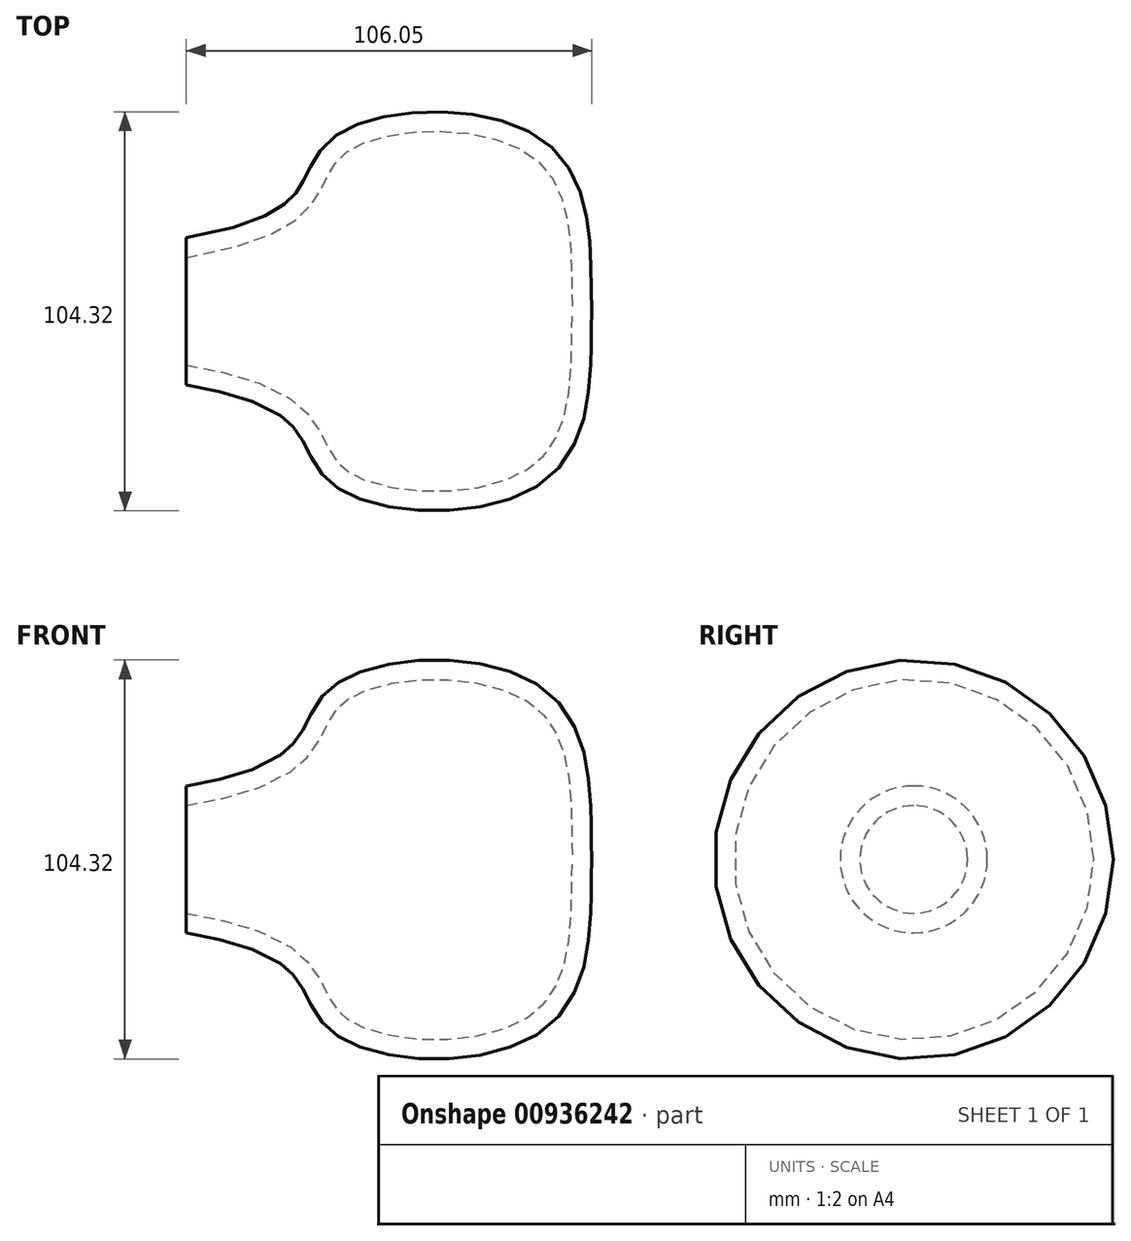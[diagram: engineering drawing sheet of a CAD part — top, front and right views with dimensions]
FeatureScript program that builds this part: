
annotation { "Feature Type Name" : "Feature", "Feature Type Description" : "" }
export const myFeature = defineFeature(function(context is Context, id is Id, definition is map)
    precondition{}
    {
        {
            var Q0;
            Q0=qCreatedBy(makeId("Top.planeOp"),FACE);
            var sketch = newSketch(context, id + "F0", { "sketchPlane" : qUnion([Q0])});
            skPoint(sketch, "E0", {"position": v(-54.13, 14.08) * mm});
            skPoint(sketch, "E1", {"position": v(-12.42, 41.47) * mm});
            skPoint(sketch, "E2", {"position": v(37.07, 39.92) * mm});
            skPoint(sketch, "E3", {"position": v(46.84, 0) * mm});
            skFitSpline(sketch, "E4", {"points": [v(-54.13, 14.08) * mm, v(-12.42, 41.47) * mm, v(37.07, 39.92) * mm, v(46.84, 0) * mm], "startDerivative": vector(352.1, 57.3) * mm, "endDerivative": vector(5.97, -126.1) * mm});
            skFitSpline(sketch, "E5", {"points": [v(-54.13, 14.08) * mm, v(-54.13, 0) * mm], "startDerivative": vector(0, -14.08) * mm, "endDerivative": vector(0, -14.08) * mm});
            skLineSegment(sketch, "E6", {"start": v(-54.13, 0) * mm, "end": v(46.84, 0) * mm});
            skSolve(sketch);
        }
        {
            var Q0;
            Q0=makeQuery(id+"F0.imprint","IMPRINT",FACE,{"disambiguationData":[TD([[makeQuery(id+"F0.imprint","IMPRINT",EDGE,{"derivedFrom":sQuery(id+"F0.wireOp",EDGE,"E4")}),-1.0]])]});
            var Q1;
            Q1=sQuery(id+"F0.wireOp",EDGE,"E6");
            revolve(context, id + "F1", {"surfaceOperationType" : NewSurfaceOperationType.NEW, "entities" : qUnion([Q0]), "axis" : qUnion([Q1]), "revolveType" : RevolveType.FULL});
        }
        {
            var Q0;
            Q0=makeQuery(id+"F1.opRevolve","SWEPT_FACE",FACE,{"disambiguationData":[OSD([sQuery(id+"F0.wireOp",EDGE,"E5")])]});
            shell(context, id + "F2", {"entities" : qUnion([Q0]), "thickness" : 5.08 * mm, "oppositeDirection" : true});
        }
    });
